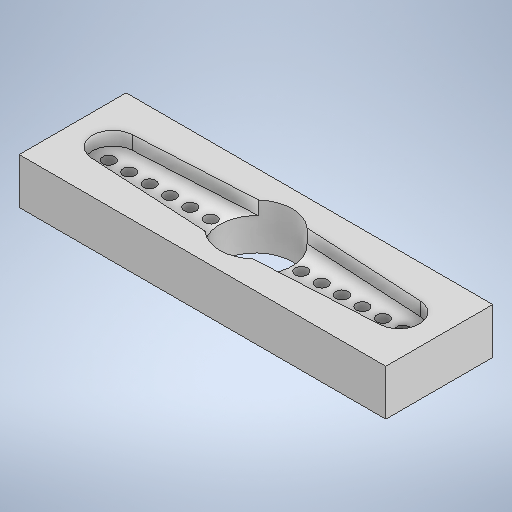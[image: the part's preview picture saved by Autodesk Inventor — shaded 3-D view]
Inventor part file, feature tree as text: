
AUTODESK INVENTOR PART (.ipt)
format: ipt  version: 2025.1 (Build 291241020, 241B)  size: 540,672 bytes
history: native  units: in
note: dims shown in document units (in); Inventor stores cm internally (conversion verified against a paired STEP export)
features: extrude x6, sketch x6, other x3
ambient origin geometry x8: Origin, YZ Plane, XZ Plane, XY Plane, X Axis, Y Axis, Z Axis, Center Point
bodies: Solid1 (feature_tree)
feature tree (15):
  other  "servoMoldAssembly.iam"
  other  "block.ipt:1"
  other  "sg90horn.ipt:1"
  extrude  "Extrusion1"  Depth=0.3937in TaperAngle=0.0deg
  extrude  "Extrusion2"  Depth=0.3937in TaperAngle=0.0deg
  extrude  "Extrusion3"  Depth=0.0591in TaperAngle=0.0deg
  extrude  "Extrusion4"  Depth=0.0591in TaperAngle=0.0deg
  extrude  "Extrusion5"  [1 undecoded]
  extrude  "Extrusion6"  [1 undecoded]
  sketch  "Sketch3"  dims[d0=0.3937in d1=0.3937in d2=0.0in]
  sketch  "Sketch4"  dims[d3=0.2795in d4=0.3937in d5=0.0in]
  sketch  "Sketch5"  dims[d6=0.0591in d7=0.0in d8=0.0591in d9=0.0in]
  sketch  "Sketch6"  dims[d10=0.0591in d11=0.0in d12=0.0591in d13=0.0in]
  sketch  "Sketch7"
  sketch  "Sketch8"
note: 2 required parameter values undecoded (feature->parameter linkage not recoverable at this tier; creation-order binding heuristic only, values carry confidence <= 0.55)
